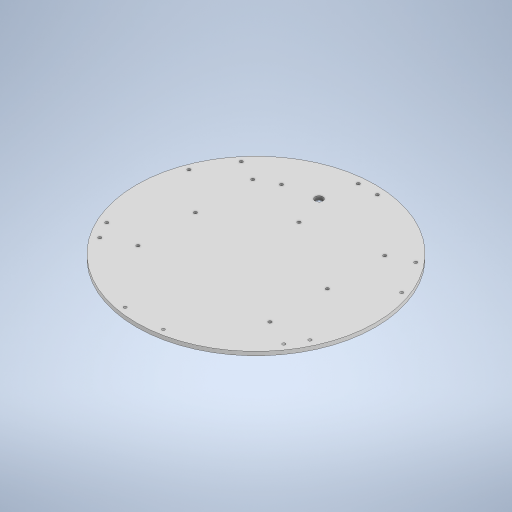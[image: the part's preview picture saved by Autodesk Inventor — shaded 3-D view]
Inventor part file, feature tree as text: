
AUTODESK INVENTOR PART (.ipt)
format: ipt  version: 2023 (Build 270158000, 158)  size: 281,088 bytes
history: native  units: mm
features: sketch x6, hole x4, extrude x2, other x1
ambient origin geometry x8: Origin, YZ Plane, XZ Plane, XY Plane, X Axis, Y Axis, Z Axis, Center Point
bodies: Body1 (feature_tree)
feature tree (13):
  other  "ソリッド1"
  extrude  "押し出し1"  Depth=250.0mm
  extrude  "押し出し2"  Depth=4.0mm TaperAngle=0.0deg
  hole  "穴1"  [1 undecoded]
  hole  "穴2"  [1 undecoded]
  hole  "穴3"  [1 undecoded]
  hole  "穴4"  [1 undecoded]
  sketch  "スケッチ1"
  sketch  "スケッチ2"
  sketch  "スケッチ4"
  sketch  "スケッチ5"
  sketch  "スケッチ6"
  sketch  "スケッチ7"
note: 4 required parameter values undecoded (feature->parameter linkage not recoverable at this tier; creation-order binding heuristic only, values carry confidence <= 0.55)
